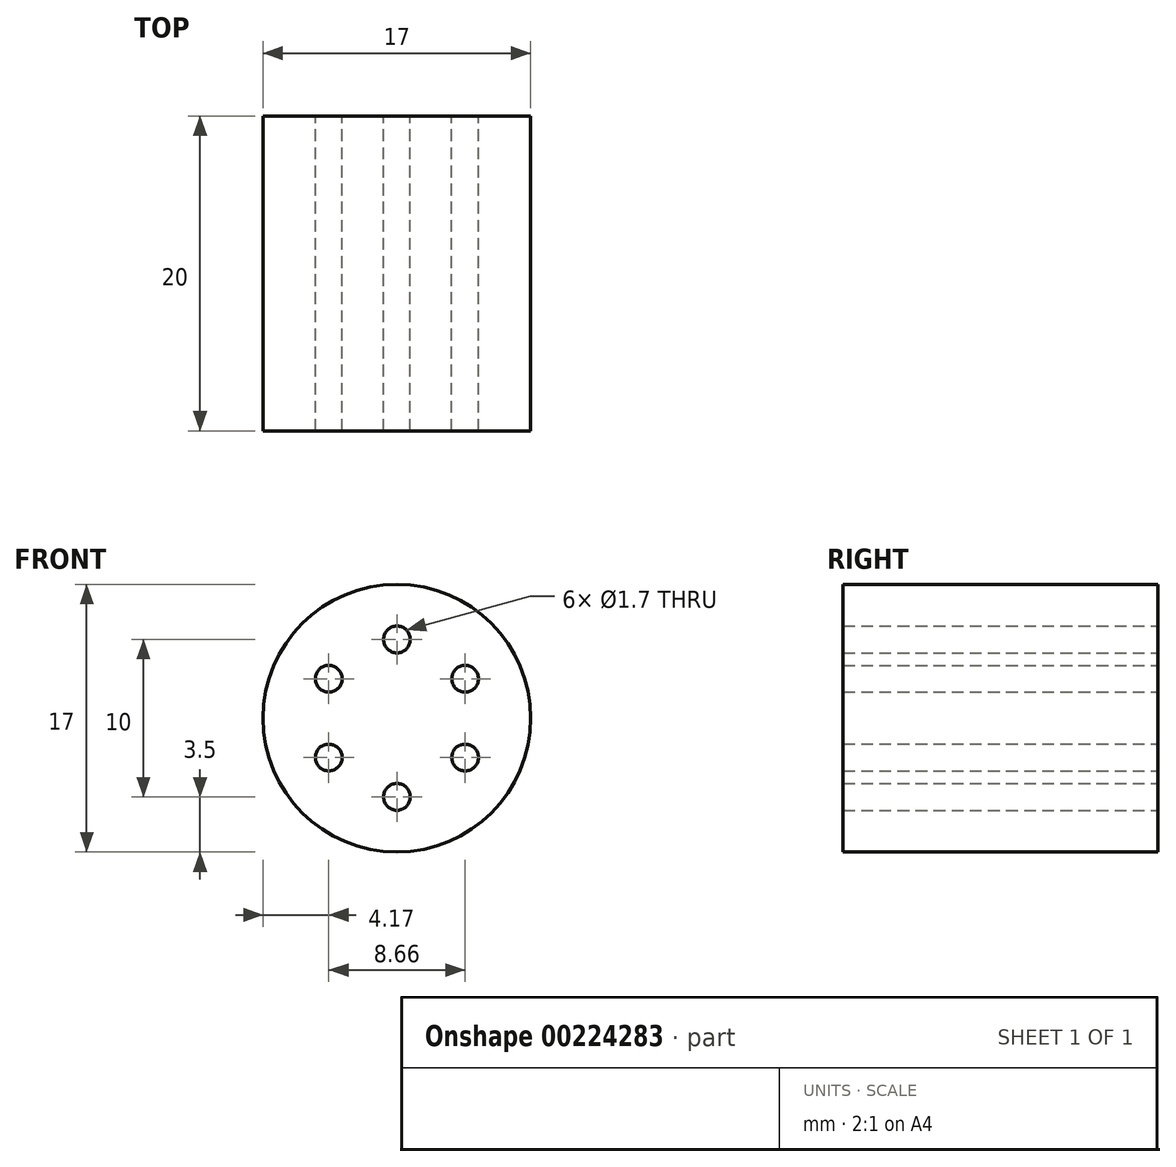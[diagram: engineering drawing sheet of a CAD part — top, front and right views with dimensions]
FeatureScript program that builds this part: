
annotation { "Feature Type Name" : "Feature", "Feature Type Description" : "" }
export const myFeature = defineFeature(function(context is Context, id is Id, definition is map)
    precondition{}
    {
        {
            var Q0;
            Q0=qCreatedBy(makeId("Front.planeOp"),FACE);
            var sketch = newSketch(context, id + "F0", { "sketchPlane" : qUnion([Q0])});
            skCircle(sketch, "E0", {"center": v(0, 0) * mm, "radius": 8.5 * mm});
            skPoint(sketch, "E1", {"position": v(0, 5) * mm});
            skCircle(sketch, "E2", {"center": v(0, 5) * mm, "radius": 0.85 * mm});
            skCircle(sketch, "E3.1.0", {"center": v(-4.33, 2.5) * mm, "radius": 0.85 * mm});
            skCircle(sketch, "E3.2.0", {"center": v(-4.33, -2.5) * mm, "radius": 0.85 * mm});
            skCircle(sketch, "E3.3.0", {"center": v(0, -5) * mm, "radius": 0.85 * mm});
            skCircle(sketch, "E3.4.0", {"center": v(4.33, -2.5) * mm, "radius": 0.85 * mm});
            skCircle(sketch, "E3.5.0", {"center": v(4.33, 2.5) * mm, "radius": 0.85 * mm});
            skSolve(sketch);
        }
        {
            var Q0;
            Q0 = qSketchRegion(id + "F0", true);
            extrude(context, id + "F1", {"entities" : qUnion([Q0]), "depth" : 20 * mm, "offsetDistance" : 25 * mm});
        }
    });
